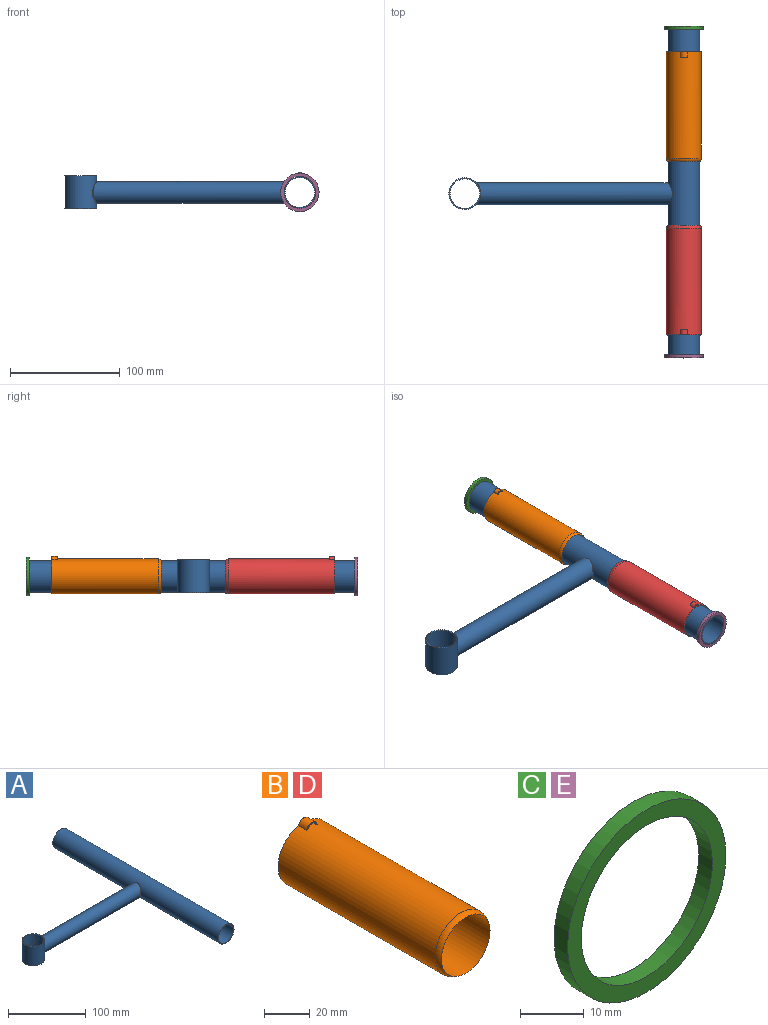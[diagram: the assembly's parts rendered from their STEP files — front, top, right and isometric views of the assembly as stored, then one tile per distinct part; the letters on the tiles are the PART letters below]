
ASSEMBLY  parts=5 mates=4
PART A: 12 faces, bbox 229x300x30 mm
  f0: cylinder r=10mm len=179mm, axis (-1,0,0), area 10985.6mm2, adj f1,f6
  f1: cylinder r=14.5mm len=30mm, axis (0,0,-1), area 2395.7mm2, adj f0,f2,f3
  f2: plane 29x29mm, normal (0,0,1), area 88mm2, adj f1,f4
  f3: plane 29x29mm, normal (0,0,-1), area 88mm2, adj f1,f4
  f4: cylinder r=13.5mm len=30mm, axis (0,0,-1), area 2544.7mm2, adj f2,f3
  f5: plane 29x29mm, normal (0,-1,0), area 88mm2, adj f6,f7
  f6: cylinder r=14.5mm len=300mm, axis (0,1,0), area 26994.6mm2, adj f0,f5,f8
  f7: cylinder r=13.5mm len=300mm, axis (0,1,0), area 25446.9mm2, adj f5,f8
  f8: plane 29x29mm, normal (0,1,0), area 88mm2, adj f6,f7
  f9: cylinder r=14.5mm len=18mm, axis (0,0,-1), area 268.7mm2, adj f10
  f10: cylinder r=9mm len=177.26mm, axis (-1,0,0), area 9841.7mm2, adj f9,f11
  f11: cylinder r=14.5mm len=18mm, axis (0,1,0), area 268.9mm2, adj f10
PART B: 7 faces, bbox 34.6x100.6x35.6 mm
  f0: cylinder r=15mm len=100mm, axis (0,1,0), area 9424.8mm2, adj f2,f6
  f1: cylinder r=16mm len=97mm, axis (0,1,0), area 9745.4mm2, adj f2,f3,f4,f5,f6
  f2: plane 34.25x32mm, normal (0,1,0), area 101.7mm2, adj f0,f1,f4,f5
  f3: plane 6.35x2.57mm, normal (0,-1,0), area 4.3mm2, adj f1,f4,f5
  f4: cylinder r=2.69mm len=5.15mm, axis (0,1,0), area 34.3mm2, adj f1,f2,f3
  f5: cylinder r=3.25mm len=6.35mm, axis (0,1,0), area 44.2mm2, adj f1,f2,f3
  f6: torus R=11mm, axis (0,-1,0), area 316.6mm2, adj f0,f1
PART C: 4 faces, bbox 35x3x35 mm
  f0: cylinder r=14.5mm len=29mm, axis (0,1,0), area 273.3mm2, adj f2,f3
  f1: cylinder r=17.5mm len=35mm, axis (0,1,0), area 329.9mm2, adj f2,f3
  f2: plane 35x35mm, normal (0,-1,0), area 301.6mm2, adj f0,f1
  f3: plane 35x35mm, normal (0,1,0), area 301.6mm2, adj f0,f1
PART D: same geometry as B
PART E: same geometry as C
PLACE A t=(-175.23,-87.68,-154.47)mm
PLACE B rot(axis=(0,-1,0),0deg) t=(24.77,41.82,-139.47)mm
PLACE C t=(24.77,65.32,-139.47)mm
PLACE D rot(axis=(0,0,-1),180deg) t=(24.77,-216.71,-139.47)mm
PLACE E t=(24.77,-234.68,-139.47)mm
MATE slider E.f1 <-> A.f6  axis (0,-1,0) through (24.77,-237.68,-139.47)mm
MATE slider D.f1 <-> A.f6  axis (0,-1,0) through (24.77,-168.21,-139.47)mm
MATE slider A.f6 <-> B.f1  axis (0,1,0) through (24.77,-87.68,-139.47)mm
MATE slider C.f1 <-> A.f6  axis (0,-1,0) through (24.77,62.32,-139.47)mm
